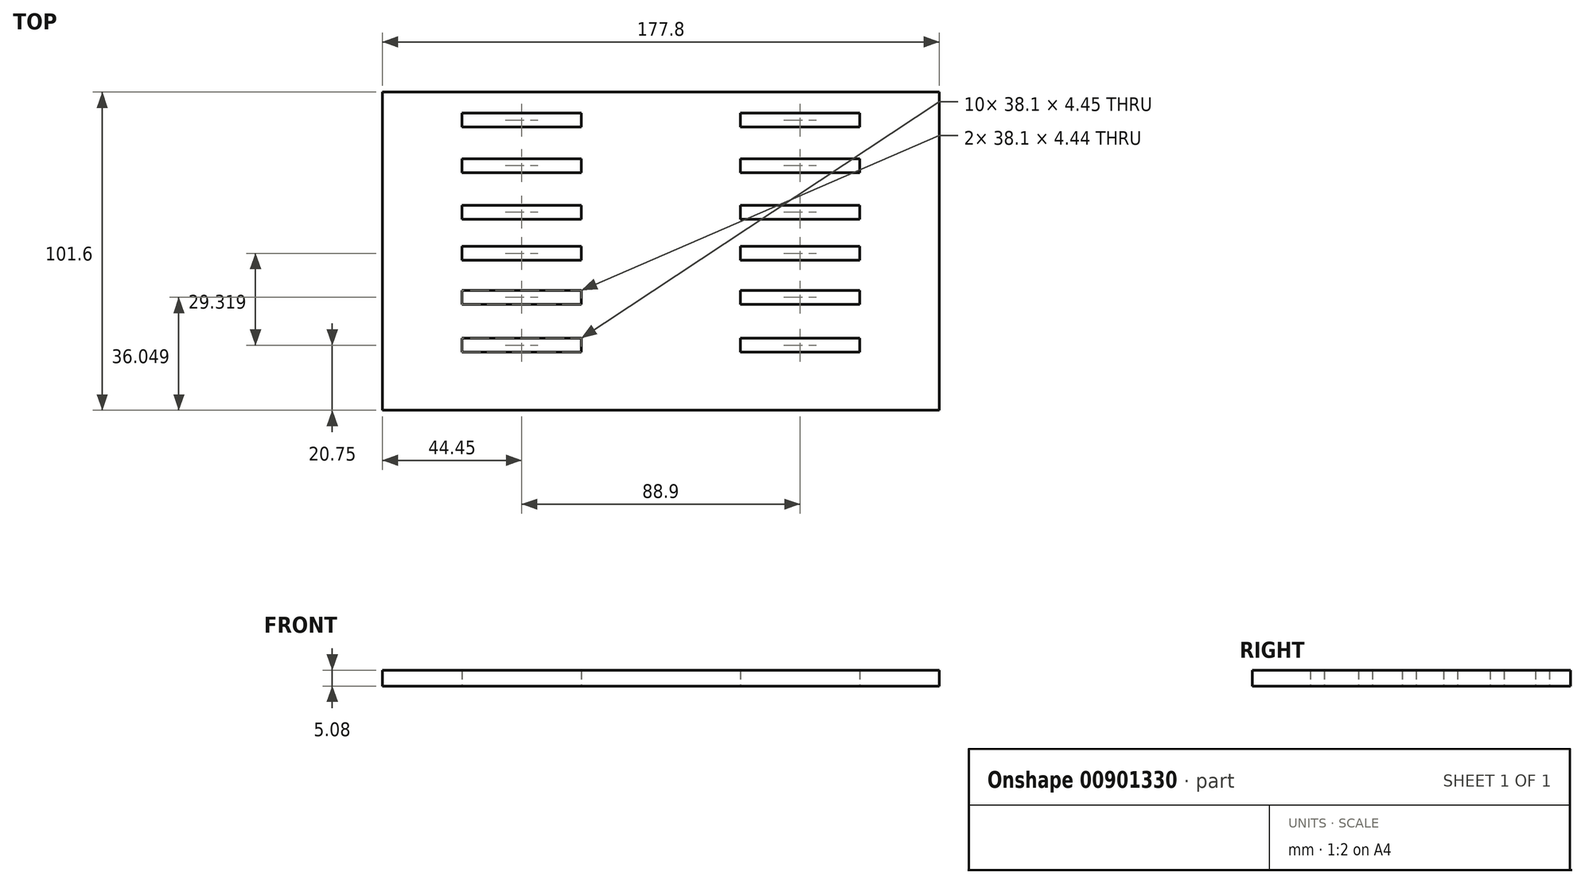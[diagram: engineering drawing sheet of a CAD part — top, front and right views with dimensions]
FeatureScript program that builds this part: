
annotation { "Feature Type Name" : "Feature", "Feature Type Description" : "" }
export const myFeature = defineFeature(function(context is Context, id is Id, definition is map)
    precondition{}
    {
        {
            var Q0;
            Q0=qCreatedBy(makeId("Top.planeOp"),FACE);
            var sketch = newSketch(context, id + "F0", { "sketchPlane" : qUnion([Q0])});
            skLineSegment(sketch, "E0.bottom", {"start": v(-88.9, 50.8) * mm, "end": v(88.9, 50.8) * mm});
            skLineSegment(sketch, "E0.top", {"start": v(-88.9, -50.8) * mm, "end": v(88.9, -50.8) * mm});
            skLineSegment(sketch, "E0.left", {"start": v(-88.9, 50.8) * mm, "end": v(-88.9, -50.8) * mm});
            skLineSegment(sketch, "E0.right", {"start": v(88.9, 50.8) * mm, "end": v(88.9, -50.8) * mm});
            skPoint(sketch, "E0.middle", {"position": v(0, 0) * mm});
            skLineSegment(sketch, "E1.MirrorCS", {"start": v(88.9, 50.8) * mm, "end": v(-88.9, 50.8) * mm});
            skLineSegment(sketch, "E2.bottom", {"start": v(-25.4, 44.03) * mm, "end": v(-63.5, 44.03) * mm});
            skLineSegment(sketch, "E2.top", {"start": v(-25.4, 39.59) * mm, "end": v(-63.5, 39.59) * mm});
            skLineSegment(sketch, "E2.left", {"start": v(-25.4, 44.03) * mm, "end": v(-25.4, 39.59) * mm});
            skLineSegment(sketch, "E2.right", {"start": v(-63.5, 44.03) * mm, "end": v(-63.5, 39.59) * mm});
            skLineSegment(sketch, "E3.bottom", {"start": v(-25.4, 29.5) * mm, "end": v(-63.5, 29.5) * mm});
            skLineSegment(sketch, "E3.top", {"start": v(-25.4, 25.06) * mm, "end": v(-63.5, 25.06) * mm});
            skLineSegment(sketch, "E3.left", {"start": v(-25.4, 29.5) * mm, "end": v(-25.4, 25.06) * mm});
            skLineSegment(sketch, "E3.right", {"start": v(-63.5, 29.5) * mm, "end": v(-63.5, 25.06) * mm});
            skLineSegment(sketch, "E4.bottom", {"start": v(-25.4, 14.68) * mm, "end": v(-63.5, 14.68) * mm});
            skLineSegment(sketch, "E4.top", {"start": v(-25.4, 10.23) * mm, "end": v(-63.5, 10.23) * mm});
            skLineSegment(sketch, "E4.left", {"start": v(-25.4, 14.68) * mm, "end": v(-25.4, 10.23) * mm});
            skLineSegment(sketch, "E4.right", {"start": v(-63.5, 14.68) * mm, "end": v(-63.5, 10.23) * mm});
            skLineSegment(sketch, "E5.bottom", {"start": v(-25.4, 1.5) * mm, "end": v(-63.5, 1.5) * mm});
            skLineSegment(sketch, "E5.top", {"start": v(-25.4, -2.95) * mm, "end": v(-63.5, -2.95) * mm});
            skLineSegment(sketch, "E5.left", {"start": v(-25.4, 1.5) * mm, "end": v(-25.4, -2.95) * mm});
            skLineSegment(sketch, "E5.right", {"start": v(-63.5, 1.5) * mm, "end": v(-63.5, -2.95) * mm});
            skLineSegment(sketch, "E6.bottom", {"start": v(-25.4, -12.53) * mm, "end": v(-63.5, -12.53) * mm});
            skLineSegment(sketch, "E6.top", {"start": v(-25.4, -16.97) * mm, "end": v(-63.5, -16.97) * mm});
            skLineSegment(sketch, "E6.left", {"start": v(-25.4, -12.53) * mm, "end": v(-25.4, -16.97) * mm});
            skLineSegment(sketch, "E6.right", {"start": v(-63.5, -12.53) * mm, "end": v(-63.5, -16.97) * mm});
            skLineSegment(sketch, "E7.bottom", {"start": v(-25.4, -27.83) * mm, "end": v(-63.5, -27.83) * mm});
            skLineSegment(sketch, "E7.top", {"start": v(-25.4, -32.27) * mm, "end": v(-63.5, -32.27) * mm});
            skLineSegment(sketch, "E7.left", {"start": v(-25.4, -27.83) * mm, "end": v(-25.4, -32.27) * mm});
            skLineSegment(sketch, "E7.right", {"start": v(-63.5, -27.83) * mm, "end": v(-63.5, -32.27) * mm});
            skLineSegment(sketch, "E8.MirrorCS", {"start": v(25.4, 44.03) * mm, "end": v(63.5, 44.03) * mm});
            skLineSegment(sketch, "E9.MirrorCS", {"start": v(63.5, 44.03) * mm, "end": v(63.5, 39.59) * mm});
            skLineSegment(sketch, "E10.MirrorCS", {"start": v(25.4, 39.59) * mm, "end": v(63.5, 39.59) * mm});
            skLineSegment(sketch, "E11.MirrorCS", {"start": v(25.4, 44.03) * mm, "end": v(25.4, 39.59) * mm});
            skLineSegment(sketch, "E12.MirrorCS", {"start": v(25.4, 29.5) * mm, "end": v(63.5, 29.5) * mm});
            skLineSegment(sketch, "E13.MirrorCS", {"start": v(25.4, 25.06) * mm, "end": v(63.5, 25.06) * mm});
            skLineSegment(sketch, "E14.MirrorCS", {"start": v(25.4, 29.5) * mm, "end": v(25.4, 25.06) * mm});
            skLineSegment(sketch, "E15.MirrorCS", {"start": v(63.5, 29.5) * mm, "end": v(63.5, 25.06) * mm});
            skLineSegment(sketch, "E16.MirrorCS", {"start": v(25.4, 14.68) * mm, "end": v(63.5, 14.68) * mm});
            skLineSegment(sketch, "E17.MirrorCS", {"start": v(25.4, 10.23) * mm, "end": v(63.5, 10.23) * mm});
            skLineSegment(sketch, "E18.MirrorCS", {"start": v(25.4, 14.68) * mm, "end": v(25.4, 10.23) * mm});
            skLineSegment(sketch, "E19.MirrorCS", {"start": v(63.5, 14.68) * mm, "end": v(63.5, 10.23) * mm});
            skLineSegment(sketch, "E20.MirrorCS", {"start": v(25.4, 1.5) * mm, "end": v(63.5, 1.5) * mm});
            skLineSegment(sketch, "E21.MirrorCS", {"start": v(25.4, -2.95) * mm, "end": v(63.5, -2.95) * mm});
            skLineSegment(sketch, "E22.MirrorCS", {"start": v(25.4, 1.5) * mm, "end": v(25.4, -2.95) * mm});
            skLineSegment(sketch, "E23.MirrorCS", {"start": v(63.5, 1.5) * mm, "end": v(63.5, -2.95) * mm});
            skLineSegment(sketch, "E24.MirrorCS", {"start": v(25.4, -12.53) * mm, "end": v(63.5, -12.53) * mm});
            skLineSegment(sketch, "E25.MirrorCS", {"start": v(25.4, -12.53) * mm, "end": v(25.4, -16.97) * mm});
            skLineSegment(sketch, "E26.MirrorCS", {"start": v(63.5, -12.53) * mm, "end": v(63.5, -16.97) * mm});
            skLineSegment(sketch, "E27.MirrorCS", {"start": v(25.4, -16.97) * mm, "end": v(63.5, -16.97) * mm});
            skLineSegment(sketch, "E28.MirrorCS", {"start": v(25.4, -27.83) * mm, "end": v(63.5, -27.83) * mm});
            skLineSegment(sketch, "E29.MirrorCS", {"start": v(25.4, -32.27) * mm, "end": v(63.5, -32.27) * mm});
            skLineSegment(sketch, "E30.MirrorCS", {"start": v(25.4, -27.83) * mm, "end": v(25.4, -32.27) * mm});
            skLineSegment(sketch, "E31.MirrorCS", {"start": v(63.5, -27.83) * mm, "end": v(63.5, -32.27) * mm});
            skSolve(sketch);
        }
        {
            var Q0;
            Q0=makeQuery(id+"F0.imprint","IMPRINT",FACE,{"disambiguationData":[TD([[makeQuery(id+"F0.imprint","IMPRINT",EDGE,{"derivedFrom":sQuery(id+"F0.wireOp",EDGE,"E0.top")}),1.0]])]});
            extrude(context, id + "F1", {"entities" : qUnion([Q0]), "depth" : 5.08 * mm, "offsetDistance" : 25.4 * mm});
        }
    });
